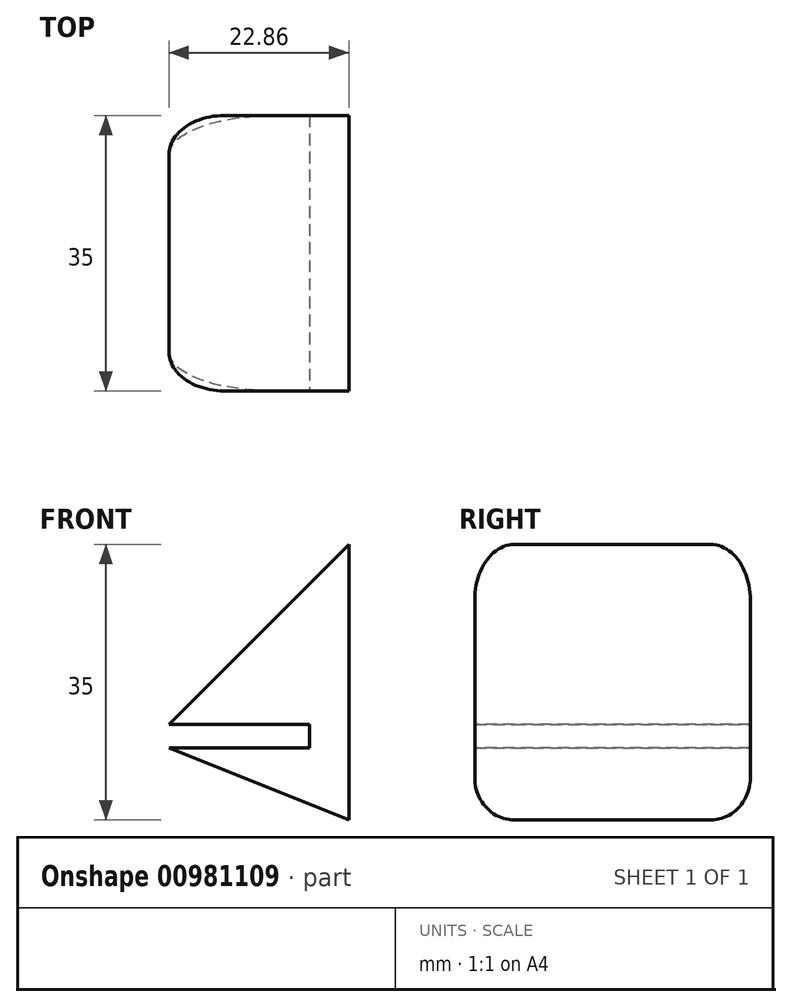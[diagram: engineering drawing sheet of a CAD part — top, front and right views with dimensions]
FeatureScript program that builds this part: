
annotation { "Feature Type Name" : "Feature", "Feature Type Description" : "" }
export const myFeature = defineFeature(function(context is Context, id is Id, definition is map)
    precondition{}
    {
        {
            var Q0;
            Q0=qCreatedBy(makeId("Front.planeOp"),FACE);
            var sketch = newSketch(context, id + "F0", { "sketchPlane" : qUnion([Q0])});
            skLineSegment(sketch, "E0", {"start": v(0, 0) * mm, "end": v(0, 35) * mm});
            skLineSegment(sketch, "E1", {"start": v(0, 35) * mm, "end": v(-25, 10) * mm});
            skLineSegment(sketch, "E2", {"start": v(-25, 10) * mm, "end": v(0, 0) * mm});
            skSolve(sketch);
        }
        {
            var Q0;
            Q0=makeQuery(id+"F0.imprint","IMPRINT",FACE,{"disambiguationData":[TD([[makeQuery(id+"F0.imprint","IMPRINT",EDGE,{"derivedFrom":sQuery(id+"F0.wireOp",EDGE,"E0")}),1.0]])]});
            extrude(context, id + "F1", {"entities" : qUnion([Q0]), "endBound" : BoundingType.SYMMETRIC, "depth" : 35 * mm, "offsetDistance" : 25 * mm});
        }
        {
            var Q0;
            Q0=makeQuery(id+"F1.opExtrude","CAP_EDGE",EDGE,{"disambiguationData":[OSD([sQuery(id+"F0.wireOp",EDGE,"E1")])],"isStart":false});
            var Q1;
            Q1=makeQuery(id+"F1.opExtrude","CAP_EDGE",EDGE,{"disambiguationData":[OSD([sQuery(id+"F0.wireOp",EDGE,"E2")])],"isStart":false});
            var Q2;
            Q2=makeQuery(id+"F1.opExtrude","CAP_EDGE",EDGE,{"disambiguationData":[OSD([sQuery(id+"F0.wireOp",EDGE,"E1")])],"isStart":true});
            var Q3;
            Q3=makeQuery(id+"F1.opExtrude","CAP_EDGE",EDGE,{"disambiguationData":[OSD([sQuery(id+"F0.wireOp",EDGE,"E2")])],"isStart":true});
            fillet(context, id + "F2", {"entities" : qUnion([Q0, Q1, Q2, Q3]), "radius" : 5 * mm, "tangentPropagation" : true, "allowEdgeOverflow" : false});
        }
        {
            var Q0;
            Q0=qCreatedBy(makeId("Front.planeOp"),FACE);
            var sketch = newSketch(context, id + "F3", { "sketchPlane" : qUnion([Q0])});
            skLineSegment(sketch, "E3.bottom", {"start": v(-45, 12.14) * mm, "end": v(-5, 12.14) * mm});
            skLineSegment(sketch, "E3.top", {"start": v(-45, 9.14) * mm, "end": v(-5, 9.14) * mm});
            skLineSegment(sketch, "E3.left", {"start": v(-45, 12.14) * mm, "end": v(-45, 9.14) * mm});
            skLineSegment(sketch, "E3.right", {"start": v(-5, 12.14) * mm, "end": v(-5, 9.14) * mm});
            skLineSegment(sketch, "E4", {"start": v(-22.86, 12.14) * mm, "end": v(-22.86, 9.14) * mm, "construction": true});
            skLineSegment(sketch, "E5", {"start": v(-22.86, 10.64) * mm, "end": v(-5, 10.64) * mm, "construction": true});
            skSolve(sketch);
        }
        {
            var Q0;
            Q0=makeQuery(id+"F3.imprint","IMPRINT",FACE,{"disambiguationData":[TD([[makeQuery(id+"F3.imprint","IMPRINT",EDGE,{"derivedFrom":sQuery(id+"F3.wireOp",EDGE,"E3.bottom")}),-1.0]])]});
            extrude(context, id + "F4", {"entities" : qUnion([Q0]), "operationType" : NewBodyOperationType.REMOVE, "endBound" : BoundingType.SYMMETRIC, "oppositeDirection" : true, "depth" : 40 * mm, "offsetDistance" : 25 * mm});
        }
    });
